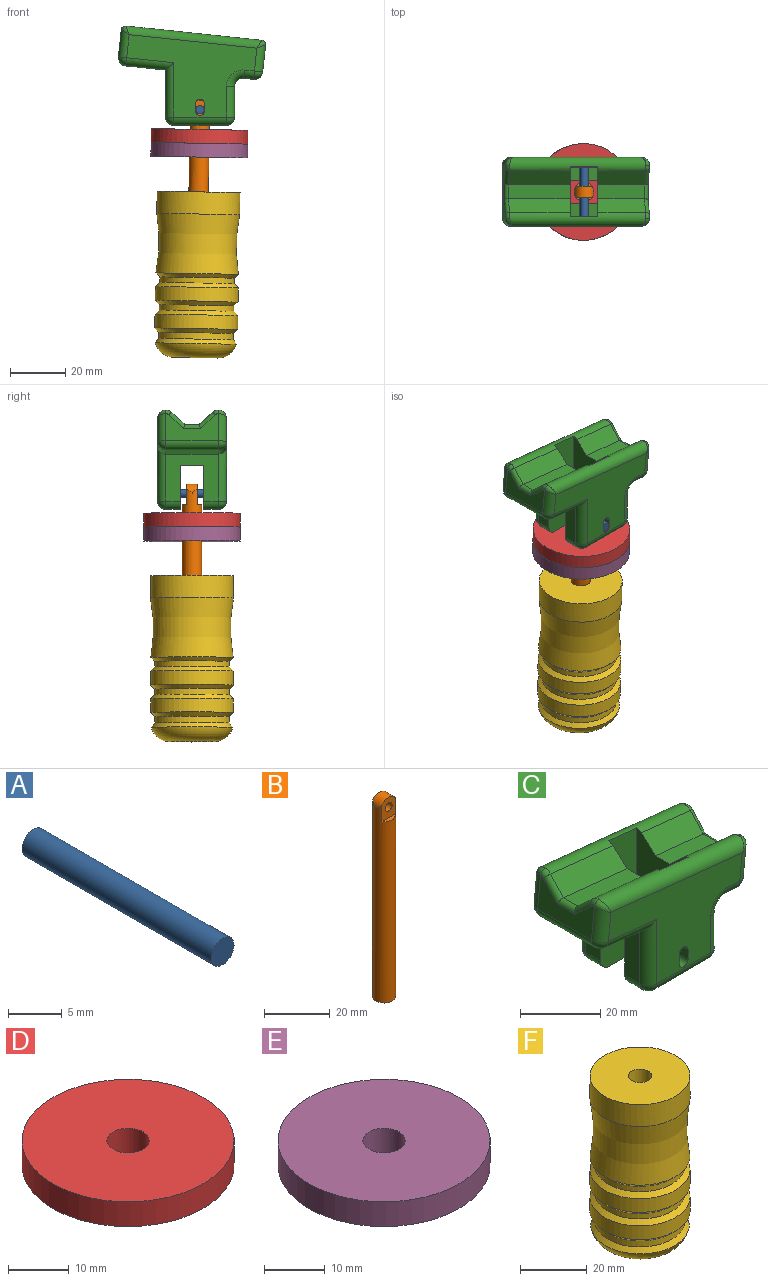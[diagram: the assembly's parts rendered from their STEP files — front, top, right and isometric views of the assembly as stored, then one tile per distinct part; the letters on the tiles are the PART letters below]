
ASSEMBLY  parts=6 mates=5
PART A: 3 faces, bbox 3x25x3 mm
  f0: cylinder r=1.5mm len=25mm, axis (0,1,0), area 235.6mm2, adj f1,f2
  f1: plane 3x3mm, normal (0,-1,0), area 7.1mm2, adj f0
  f2: plane 3x3mm, normal (0,1,0), area 7.1mm2, adj f0
PART B: 8 faces, bbox 7x7x75 mm
  f0: cylinder r=3.5mm len=73.5mm, axis (0,0,-1), area 1527.3mm2, adj f1,f2,f3,f4,f5,f6
  f1: plane 7.5x5.74mm, normal (0,1,0), area 33.4mm2, adj f0,f4,f6,f7
  f2: plane 7.5x5.74mm, normal (0,-1,0), area 33.4mm2, adj f0,f5,f6,f7
  f3: plane 7x7mm, normal (0,0,-1), area 38.5mm2, adj f0
  f4: plane 5.74x1.5mm, normal (0,0,1), area 6mm2, adj f0,f1
  f5: plane 5.74x1.5mm, normal (0,0,1), area 6mm2, adj f0,f2
  f6: cylinder r=3.5mm len=7mm, axis (0,-1,0), area 35.7mm2, adj f0,f1,f2
  f7: cylinder r=1.5mm len=4mm, axis (0,-1,0), area 37.7mm2, adj f1,f2
PART C: 84 faces, bbox 53.4x25x36.2 mm
  f0: plane 25.73x16mm, normal (0,-1,0), area 300.6mm2, adj f7,f9,f15,f17,f18,f19,f20,f21
  f1: plane 25.73x16mm, normal (0,1,0), area 300.6mm2, adj f4,f8,f15,f16,f18,f21,f22,f43
  f2: plane 47.12x29.81mm, normal (0,-1,0), area 738.2mm2, adj f13,f37,f42,f46,f48,f49,f52,f57
  f3: plane 47.12x29.81mm, normal (0,1,0), area 738.2mm2, adj f14,f44,f55,f56,f60,f61,f64,f66
  f4: plane 4.75x3.5mm, normal (0,0,1), area 16.6mm2, adj f1,f5,f74,f81
  f5: plane 26.12x10mm, normal (0,1,0), area 250.9mm2, adj f4,f8,f13,f74,f75,f81,f82,f83
  f6: plane 26.12x10mm, normal (0,-1,0), area 250.9mm2, adj f7,f9,f14,f74,f75,f77,f78,f79
  f7: plane 4.75x3.5mm, normal (0,0,1), area 16.6mm2, adj f0,f6,f74,f77
  f8: plane 4.75x3.5mm, normal (0,0,1), area 16.6mm2, adj f1,f5,f75,f82
  f9: plane 4.75x3.5mm, normal (0,0,1), area 16.6mm2, adj f0,f6,f75,f78
  f10: plane 17.31x6.32mm, normal (0.08,0.67,0.74), area 115.5mm2, adj f12,f13,f33,f74
  f11: plane 17.31x6.32mm, normal (0.08,-0.67,0.74), area 115.5mm2, adj f12,f14,f31,f74
  f12: plane 16.83x5mm, normal (0.1,0,0.99), area 84.6mm2, adj f10,f11,f32,f74
  f13: cylinder r=3mm len=49.54mm, axis (-0.99,0,0.1), area 320.3mm2, adj f2,f5,f10,f28,f39,f41,f47,f53
  f14: cylinder r=3mm len=49.54mm, axis (-0.99,0,0.1), area 320.3mm2, adj f3,f6,f11,f29,f68,f69,f71,f72
  f15: plane 8.5x8.23mm, normal (0,0,-1), area 69.9mm2, adj f0,f1,f21,f74
  f16: plane 19x5.25mm, normal (0,0,-1), area 99.8mm2, adj f1,f37,f43,f45
  f17: plane 11.04x5.25mm, normal (1,0,0), area 58mm2, adj f0,f20,f21,f56
  f18: plane 19x17mm, normal (-1,0,0), area 212.5mm2, adj f0,f1,f19,f25,f42,f43,f55,f73
  f19: cylinder r=3mm len=5.25mm, axis (0,-1,0), area 24.7mm2, adj f0,f18,f23,f50
  f20: cylinder r=3mm len=5.25mm, axis (0,1,0), area 24.7mm2, adj f0,f17,f23,f51
  f21: cylinder r=3mm len=19mm, axis (0,-1,0), area 77.4mm2, adj f0,f1,f15,f17,f22,f24,f52,f61
  f22: plane 11.04x5.25mm, normal (1,0,0), area 58mm2, adj f1,f21,f45,f46
  f23: plane 19x5.25mm, normal (0,0,-1), area 99.7mm2, adj f0,f19,f20,f44
  f24: plane 19x3.58mm, normal (-0.1,0,-0.99), area 68.4mm2, adj f21,f57,f64,f65
  f25: plane 19x14.35mm, normal (-0.1,0,-0.99), area 274.2mm2, adj f18,f49,f59,f60
  f26: plane 19x9.81mm, normal (0.99,0,-0.1), area 123.8mm2, adj f31,f32,f33,f47,f58,f65,f70,f72
  f27: plane 19x9.81mm, normal (-0.99,0,0.1), area 123.8mm2, adj f34,f35,f36,f39,f48,f59,f66,f68
  f28: plane 22.4x6.85mm, normal (0.08,0.67,0.74), area 149.9mm2, adj f13,f30,f36,f75
  f29: plane 22.4x6.85mm, normal (0.08,-0.67,0.74), area 149.9mm2, adj f14,f30,f34,f75
  f30: plane 22.4x5mm, normal (0.1,0,0.99), area 112.6mm2, adj f28,f29,f35,f75
  f31: cylinder r=1.5mm len=6.42mm, axis (-0.07,-0.74,-0.67), area 16.4mm2, adj f11,f26,f32,f72
  f32: cylinder r=1.5mm len=6.16mm, axis (0,-1,0), area 12.8mm2, adj f12,f26,f31,f33
  f33: cylinder r=1.5mm len=6.42mm, axis (0.07,-0.74,0.67), area 16.4mm2, adj f10,f26,f32,f47
  f34: cylinder r=1.5mm len=6.42mm, axis (0.07,0.74,0.67), area 16.4mm2, adj f27,f29,f35,f68
  f35: cylinder r=1.5mm len=6.16mm, axis (0,1,0), area 12.8mm2, adj f27,f30,f34,f36
  f36: cylinder r=1.5mm len=6.42mm, axis (-0.07,0.74,-0.67), area 16.4mm2, adj f27,f28,f35,f39
  f37: cylinder r=3mm len=19mm, axis (1,0,0), area 89.5mm2, adj f2,f16,f38,f40
  f38: sphere r=3mm, area 14.1mm2, adj f37,f42,f43
  f39: torus R=1.5mm, axis (-0.99,0,0.1), area 4.3mm2, adj f13,f27,f36,f41
  f40: sphere r=3mm, area 14.1mm2, adj f37,f45,f46
  f41: bspline ~3.58x3.3mm, area 7.4mm2, adj f13,f39,f48
  f42: cylinder r=3mm len=19.7mm, axis (0,0,-1), area 84.7mm2, adj f2,f18,f38,f49
  f43: cylinder r=3mm len=5.25mm, axis (0,-1,0), area 24.7mm2, adj f1,f16,f18,f38
  f44: cylinder r=3mm len=19mm, axis (-1,0,0), area 89.5mm2, adj f3,f23,f50,f51
  f45: cylinder r=3mm len=5.25mm, axis (0,1,0), area 24.7mm2, adj f1,f16,f22,f40
  f46: cylinder r=3mm len=11.04mm, axis (0,0,1), area 52mm2, adj f2,f22,f40,f52
  f47: torus R=1.5mm, axis (-0.99,0,0.1), area 4.3mm2, adj f13,f26,f33,f53
  f48: cylinder r=3mm len=10.13mm, axis (0.1,0,0.99), area 43.9mm2, adj f2,f27,f41,f54
  f49: cylinder r=3mm len=17.35mm, axis (-0.99,0,0.1), area 72.6mm2, adj f2,f25,f42,f54
  f50: sphere r=3mm, area 14.1mm2, adj f19,f44,f55
  f51: sphere r=3mm, area 14.1mm2, adj f20,f44,f56
  f52: torus R=6mm, axis (0,-1,0), area 32.3mm2, adj f2,f21,f46,f57
  f53: bspline ~3.3x3.15mm, area 7.4mm2, adj f13,f47,f58
  f54: sphere r=3mm, area 14.1mm2, adj f48,f49,f59
  f55: cylinder r=3mm len=19.7mm, axis (0,0,1), area 84.7mm2, adj f3,f18,f50,f60
  f56: cylinder r=3mm len=11.04mm, axis (0,0,-1), area 52mm2, adj f3,f17,f51,f61
  f57: cylinder r=3mm len=3.89mm, axis (-0.99,0,0.1), area 17mm2, adj f2,f24,f52,f62
  f58: cylinder r=3mm len=10.13mm, axis (-0.1,0,-0.99), area 43.9mm2, adj f2,f26,f53,f62
  f59: cylinder r=3mm len=19mm, axis (0,-1,0), area 89.5mm2, adj f25,f27,f54,f63
  f60: cylinder r=3mm len=17.35mm, axis (0.99,0,-0.1), area 72.6mm2, adj f3,f25,f55,f63
  f61: torus R=6mm, axis (0,-1,0), area 32.3mm2, adj f3,f21,f56,f64
  f62: sphere r=3mm, area 14.1mm2, adj f57,f58,f65
  f63: sphere r=3mm, area 14.1mm2, adj f59,f60,f66
  f64: cylinder r=3mm len=3.89mm, axis (0.99,0,-0.1), area 17mm2, adj f3,f24,f61,f67
  f65: cylinder r=3mm len=19mm, axis (0,1,0), area 89.5mm2, adj f24,f26,f62,f67
  f66: cylinder r=3mm len=10.13mm, axis (-0.1,0,-0.99), area 43.9mm2, adj f3,f27,f63,f69
  f67: sphere r=3mm, area 14.1mm2, adj f64,f65,f70
  f68: torus R=1.5mm, axis (-0.99,0,0.1), area 4.3mm2, adj f14,f27,f34,f69
  f69: bspline ~3.58x3.3mm, area 7.4mm2, adj f14,f66,f68
  f70: cylinder r=3mm len=10.13mm, axis (0.1,0,0.99), area 43.9mm2, adj f3,f26,f67,f71
  f71: bspline ~3.58x3.3mm, area 7.4mm2, adj f14,f70,f72
  f72: torus R=1.5mm, axis (-0.99,0,0.1), area 4.3mm2, adj f14,f26,f31,f71
  f73: plane 8.5x7.5mm, normal (0,0,-1), area 63.7mm2, adj f0,f1,f18,f75
  f74: plane 25.07x18mm, normal (-1,0,0), area 321.6mm2, adj f0,f1,f4,f5,f6,f7,f10,f11
  f75: plane 26.12x18mm, normal (1,0,0), area 340.5mm2, adj f0,f1,f5,f6,f8,f9,f13,f14
  f76: cylinder r=1.5mm len=8.25mm, axis (0,-1,0), area 38.9mm2, adj f0,f3,f77,f78
  f77: plane 8.25x3mm, normal (-1,0,0), area 22.4mm2, adj f0,f3,f6,f7,f76,f79
  f78: plane 8.25x3mm, normal (1,0,0), area 22.4mm2, adj f0,f3,f6,f9,f76,f79
  f79: cylinder r=1.5mm len=3.5mm, axis (0,-1,0), area 16.5mm2, adj f3,f6,f77,f78
  f80: cylinder r=1.5mm len=8.25mm, axis (0,-1,0), area 38.9mm2, adj f1,f2,f81,f82
  f81: plane 8.25x3mm, normal (-1,0,0), area 22.4mm2, adj f1,f2,f4,f5,f80,f83
  f82: plane 8.25x3mm, normal (1,0,0), area 22.4mm2, adj f1,f2,f5,f8,f80,f83
  f83: cylinder r=1.5mm len=3.5mm, axis (0,-1,0), area 16.5mm2, adj f2,f5,f81,f82
PART D: 4 faces, bbox 35x35x5 mm
  f0: cylinder r=17.5mm len=35mm, axis (0,0,-1), area 549.8mm2, adj f1,f2
  f1: plane 35x35mm, normal (0,0,1), area 923.6mm2, adj f0,f3
  f2: plane 35x35mm, normal (0,0,-1), area 923.6mm2, adj f0,f3
  f3: cylinder r=3.5mm len=7mm, axis (0,0,-1), area 110mm2, adj f1,f2
PART E: 4 faces, bbox 35x35x5 mm
  f0: cylinder r=17.5mm len=35mm, axis (0,0,-1), area 549.8mm2, adj f1,f2
  f1: plane 35x35mm, normal (0,0,1), area 923.6mm2, adj f0,f3
  f2: plane 35x35mm, normal (0,0,-1), area 923.6mm2, adj f0,f3
  f3: cylinder r=3.5mm len=7mm, axis (0,0,-1), area 110mm2, adj f1,f2
PART F: 18 faces, bbox 67.9x67.9x85.2 mm
  f0: cylinder r=15mm len=30mm, axis (0,0,-1), area 754mm2, adj f1,f4
  f1: plane 30x30mm, normal (0,0,1), area 668.4mm2, adj f0,f2
  f2: cylinder r=3.5mm len=55mm, axis (0,0,-1), area 1209.5mm2, adj f1,f3
  f3: plane 7x7mm, normal (0,0,1), area 38.5mm2, adj f2
  f4: torus R=73.98mm, axis (0,0,-1), area 1950.7mm2, adj f0,f14
  f5: cylinder r=13.5mm len=27mm, axis (0,0,-1), area 169.6mm2, adj f14,f17
  f6: cylinder r=15mm len=30mm, axis (0,0,-1), area 471.2mm2, adj f13,f17
  f7: cylinder r=13.5mm len=27mm, axis (0,0,-1), area 169.6mm2, adj f13,f16
  f8: cylinder r=15mm len=30mm, axis (0,0,-1), area 471.2mm2, adj f12,f16
  f9: cylinder r=13.5mm len=27mm, axis (0,0,-1), area 193mm2, adj f12,f15
  f10: plane 16x16mm, normal (0,0,-1), area 201.1mm2, adj f11
  f11: torus R=8mm, axis (0,0,1), area 679.4mm2, adj f10,f15
  f12: cone r=13.5mm half-angle=45deg, axis (0,0,1), area 189.9mm2, adj f8,f9
  f13: cone r=13.5mm half-angle=45deg, axis (0,0,1), area 189.9mm2, adj f6,f7
  f14: cone r=13.5mm half-angle=45deg, axis (0,0,1), area 179.7mm2, adj f4,f5
  f15: cone r=13.29mm half-angle=37.1deg, axis (0,0,-1), area 181.6mm2, adj f9,f11
  f16: cone r=15mm half-angle=45deg, axis (0,0,-1), area 189.9mm2, adj f7,f8
  f17: cone r=15mm half-angle=45deg, axis (0,0,-1), area 189.9mm2, adj f5,f6
PLACE A rot(axis=(0,-1,0),148.1deg) t=(40.65,24.74,90.84)mm
PLACE B rot(axis=(0.01,0,1),180deg) t=(15.26,24.74,4.87)mm
PLACE C t=(16.07,24.74,5.69)mm fixed
PLACE D rot(axis=(0.01,0.04,1),23.8deg) t=(15.24,24.74,4.21)mm
PLACE E rot(axis=(-0.01,0,-1),156.4deg) t=(15.24,24.74,4.22)mm
PLACE F rot(axis=(-0.01,0.01,-1),117.7deg) t=(15.02,24.74,-8.39)mm
MATE revolute A.f0 <-> B.f6  axis (0,1,0) through (16.07,24.74,51.37)mm
MATE pin_slot A.f0 <-> C.f79  axis (0,-1,0) through (16.07,12.24,51.37)mm
MATE cylindrical D.f0 <-> B.f0  axis (0.02,0,1) through (15.94,24.74,44.21)mm
MATE cylindrical E.f0 <-> B.f0  axis (0.02,0,1) through (15.86,24.74,39.21)mm
MATE cylindrical F.f0 <-> B.f0  axis (0.02,0,1) through (15.55,24.74,21.6)mm
